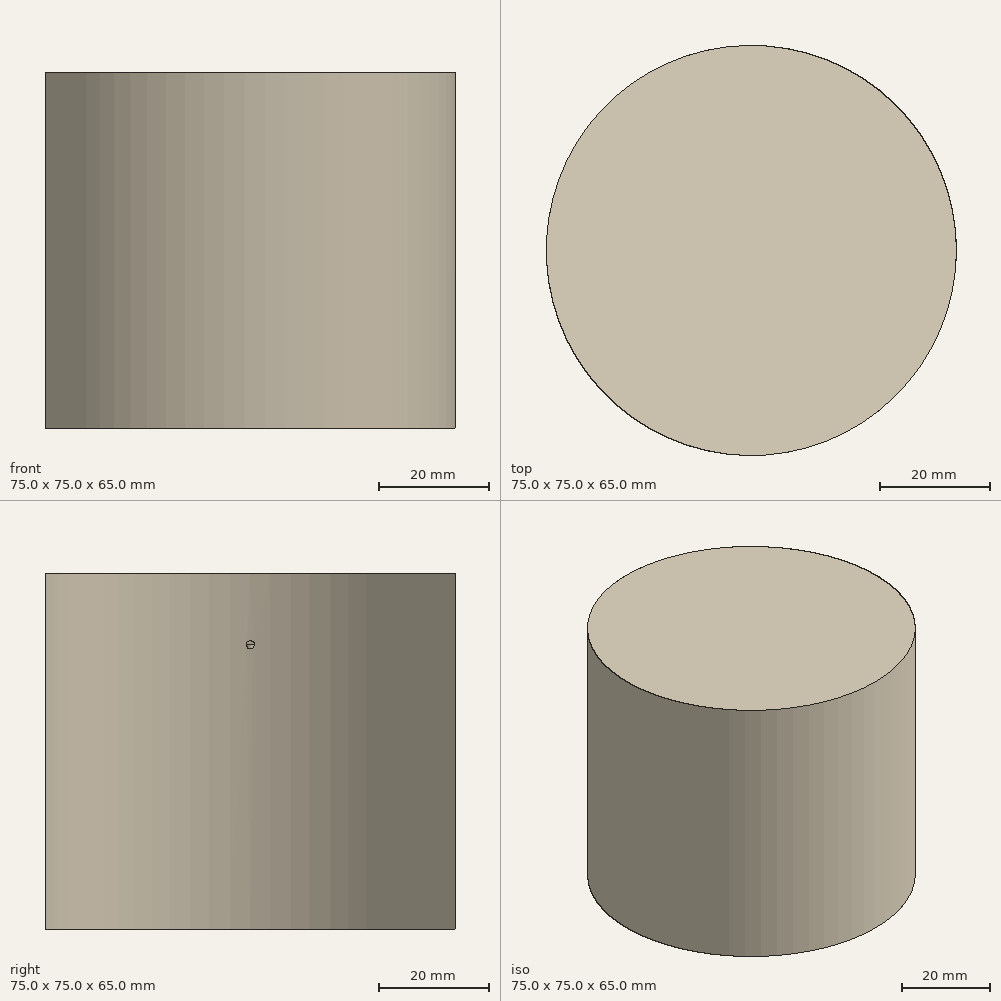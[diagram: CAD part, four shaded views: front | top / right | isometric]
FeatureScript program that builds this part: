
annotation { "Feature Type Name" : "Feature", "Feature Type Description" : "" }
export const myFeature = defineFeature(function(context is Context, id is Id, definition is map)
    precondition{}
    {
        {
            var Q0;
            Q0=qCreatedBy(makeId("Top.planeOp"),FACE);
            var sketch = newSketch(context, id + "F0", { "sketchPlane" : qUnion([Q0])});
            skCircle(sketch, "E0", {"center": v(0, 0) * mm, "radius": 37.5 * mm});
            skLineSegment(sketch, "E1", {"start": v(-37.5, 0) * mm, "end": v(37.5, 0) * mm});
            skCircle(sketch, "E2", {"center": v(-19.5, 0) * mm, "radius": 10 * mm});
            skCircle(sketch, "E3", {"center": v(19.5, 0) * mm, "radius": 10 * mm});
            skCircle(sketch, "E4", {"center": v(0, 0) * mm, "radius": 3 * mm});
            skPoint(sketch, "E5", {"position": v(37.5, 0) * mm});
            skSolve(sketch);
        }
        {
            var Q0;
            Q0=makeQuery(id+"F0.imprint","IMPRINT",FACE,{"disambiguationData":[TD([[makeQuery(id+"F0.imprint","IMPRINT",EDGE,{"derivedFrom":sQuery(id+"F0.wireOp",EDGE,"E0")}),1.0]])]});
            extrude(context, id + "F1", {"entities" : qUnion([Q0]), "depth" : 40 * mm});
        }
        {
            var Q0;
            Q0=makeQuery(id+"F1.opExtrude","CAP_FACE",FACE,{"disambiguationData":[OSD([sQuery(id+"F0.wireOp",EDGE,"E0"),sQuery(id+"F0.wireOp",EDGE,"E2"),sQuery(id+"F0.wireOp",EDGE,"E3"),sQuery(id+"F0.wireOp",EDGE,"E4")])],"isStart":false});
            var sketch = newSketch(context, id + "F2", { "sketchPlane" : qUnion([Q0])});
            skCircle(sketch, "E6", {"center": v(0, 0) * mm, "radius": 37.5 * mm});
            skSolve(sketch);
        }
        {
            var Q0;
            Q0 = qSketchRegion(id + "F2", true);
            extrude(context, id + "F3", {"entities" : qUnion([Q0]), "operationType" : NewBodyOperationType.ADD, "depth" : 25 * mm});
        }
        {
            var Q0;
            Q0=makeQuery(id+"F3.boolean.opBoolean","SPLIT",FACE,{"disambiguationData":[TD([makeQuery(id+"F1.opExtrude","SWEPT_FACE",FACE,{"disambiguationData":[OSD([sQuery(id+"F0.wireOp",EDGE,"E3")])]})])],"derivedFrom":makeQuery(id+"F3.opExtrude","CAP_FACE",FACE,{"disambiguationData":[OSD([sQuery(id+"F2.wireOp",EDGE,"E6")])],"isStart":true})});
            var sketch = newSketch(context, id + "F4", { "sketchPlane" : qUnion([Q0])});
            skCircle(sketch, "E7", {"center": v(19.5, 0) * mm, "radius": 0.75 * mm});
            skSolve(sketch);
        }
        {
            var Q0;
            Q0 = qSketchRegion(id + "F4", true);
            extrude(context, id + "F5", {"entities" : qUnion([Q0]), "operationType" : NewBodyOperationType.REMOVE, "oppositeDirection" : true, "depth" : 12 * mm});
        }
        {
            var Q0;
            Q0=qCreatedBy(makeId("Right.planeOp"),FACE);
            var Q1;
            Q1=sQuery(id+"F0.wireOp",VERTEX,"E5");
            cPlane(context, id + "F6", {"entities" : qUnion([Q0, Q1]), "cplaneType" : CPlaneType.PLANE_POINT, "offset" : 25 * mm, "width" : 150 * mm, "height" : 150 * mm});
        }
        {
            var Q0;
            Q0=qCreatedBy(makeId("Top.planeOp"),FACE);
            var sketch = newSketch(context, id + "F7", { "sketchPlane" : qUnion([Q0])});
            skLineSegment(sketch, "E8", {"start": v(29.5, 0) * mm, "end": v(9.5, 0) * mm, "construction": true});
            skPoint(sketch, "E9", {"position": v(19.5, 0) * mm});
            skSolve(sketch);
        }
        {
            var Q0;
            Q0=qCreatedBy(makeId("Front.planeOp"),FACE);
            var sketch = newSketch(context, id + "F8", { "sketchPlane" : qUnion([Q0])});
            skLineSegment(sketch, "E10", {"start": v(19.5, 0) * mm, "end": v(19.5, 52) * mm, "construction": true});
            skSolve(sketch);
        }
        {
            var Q0;
            Q0=qCreatedBy(makeId("Right.planeOp"),FACE);
            var Q1;
            Q1=sQuery(id+"F8.wireOp",VERTEX,"E10.end");
            cPlane(context, id + "F9", {"entities" : qUnion([Q0, Q1]), "cplaneType" : CPlaneType.PLANE_POINT, "offset" : 25 * mm, "width" : 150 * mm, "height" : 150 * mm});
        }
        {
            var Q0;
            Q0=qCreatedBy(id+"F9.planeOp",FACE);
            var sketch = newSketch(context, id + "F10", { "sketchPlane" : qUnion([Q0])});
            skCircle(sketch, "E11", {"center": v(0, 52) * mm, "radius": 0.75 * mm});
            skSolve(sketch);
        }
        {
            var Q0;
            Q0 = qSketchRegion(id + "F10", true);
            extrude(context, id + "F11", {"entities" : qUnion([Q0]), "operationType" : NewBodyOperationType.REMOVE, "endBound" : BoundingType.THROUGH_ALL, "depth" : 25 * mm});
        }
    });
